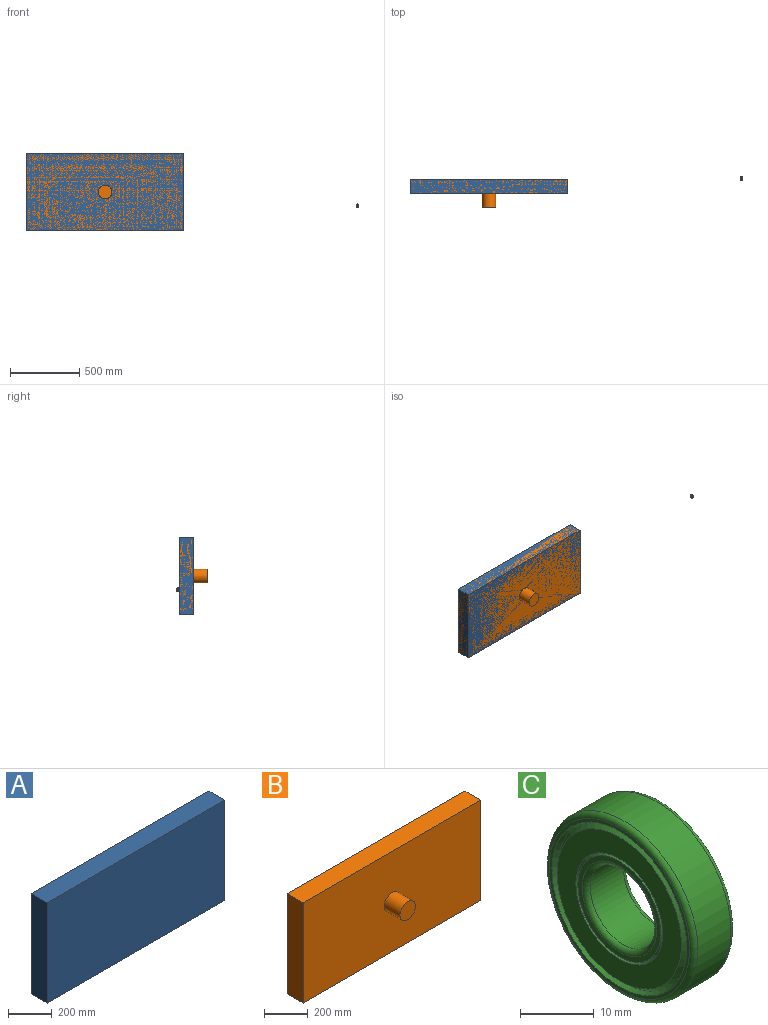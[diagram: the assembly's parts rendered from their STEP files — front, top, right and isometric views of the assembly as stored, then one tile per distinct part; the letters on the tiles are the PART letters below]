
ASSEMBLY  parts=3 mates=2
PART A: 6 faces, bbox 1143x101.6x558.8 mm
  f0: plane 558.8x101.6mm, normal (-1,0,0), area 56774.1mm2, adj f1,f3,f4,f5
  f1: plane 1143x101.6mm, normal (0,0,-1), area 116128.8mm2, adj f0,f2,f4,f5
  f2: plane 558.8x101.6mm, normal (1,0,0), area 56774.1mm2, adj f1,f3,f4,f5
  f3: plane 1143x101.6mm, normal (0,0,1), area 116128.8mm2, adj f0,f2,f4,f5
  f4: plane 1143x558.8mm, normal (0,-1,0), area 638708.4mm2, adj f0,f1,f2,f3
  f5: plane 1143x558.8mm, normal (0,1,0), area 638708.4mm2, adj f0,f1,f2,f3
PART B: 8 faces, bbox 1143x203.2x558.8 mm
  f0: plane 558.8x101.6mm, normal (-1,0,0), area 56774.1mm2, adj f1,f3,f4,f5
  f1: plane 1143x101.6mm, normal (0,0,-1), area 116128.8mm2, adj f0,f2,f4,f5
  f2: plane 558.8x101.6mm, normal (1,0,0), area 56774.1mm2, adj f1,f3,f4,f5
  f3: plane 1143x101.6mm, normal (0,0,1), area 116128.8mm2, adj f0,f2,f4,f5
  f4: plane 1143x558.8mm, normal (0,-1,0), area 630867.7mm2, adj f0,f1,f2,f3,f6
  f5: plane 1143x558.8mm, normal (0,1,0), area 638708.4mm2, adj f0,f1,f2,f3
  f6: cylinder r=49.96mm len=101.6mm, axis (0,1,0), area 31891.6mm2, adj f4,f7
  f7: plane 99.92x99.92mm, normal (0,-1,0), area 7840.7mm2, adj f6
PART C: 20 faces, bbox 7.9x30.9x30.9 mm
  f0: cone r=12.95mm half-angle=27.8deg, axis (1,0,0), area 65.6mm2, adj f1,f15
  f1: cone r=12.57mm half-angle=41.3deg, axis (-1,0,0), area 74.1mm2, adj f0,f14
  f2: cone r=7.97mm half-angle=26.6deg, axis (-1,0,0), area 21.6mm2, adj f3,f18
  f3: cone r=8.16mm half-angle=26.6deg, axis (1,0,0), area 22.1mm2, adj f2,f14
  f4: cone r=12.95mm half-angle=27.8deg, axis (-1,0,0), area 65.6mm2, adj f5,f17
  f5: cone r=12.57mm half-angle=41.3deg, axis (1,0,0), area 74.1mm2, adj f4,f16
  f6: cone r=7.97mm half-angle=26.6deg, axis (1,0,0), area 21.6mm2, adj f7,f19
  f7: cone r=8.16mm half-angle=26.6deg, axis (-1,0,0), area 22.1mm2, adj f6,f16
  f8: torus R=13.49mm, axis (1,0,0), area 109.7mm2, adj f13,f15
  f9: torus R=7.14mm, axis (1,0,0), area 52mm2, adj f12,f18
  f10: torus R=7.14mm, axis (1,0,0), area 52mm2, adj f12,f19
  f11: torus R=13.49mm, axis (1,0,0), area 109.7mm2, adj f13,f17
  f12: cylinder r=6.35mm len=12.7mm, axis (1,0,0), area 253.4mm2, adj f9,f10
  f13: cylinder r=14.29mm len=28.58mm, axis (-1,0,0), area 570mm2, adj f8,f11
  f14: plane 23.88x23.88mm, normal (1,0,0), area 228.6mm2, adj f1,f3
  f15: plane 26.99x26.99mm, normal (1,0,0), area 44.8mm2, adj f0,f8
  f16: plane 23.88x23.88mm, normal (-1,0,0), area 228.6mm2, adj f5,f7
  f17: plane 26.99x26.99mm, normal (-1,0,0), area 44.8mm2, adj f4,f11
  f18: plane 15.94x15.94mm, normal (1,0,0), area 39.3mm2, adj f2,f9
  f19: plane 15.94x15.94mm, normal (-1,0,0), area 39.3mm2, adj f6,f10
PLACE A rot(axis=(0,1,0),180deg) t=(-1781.45,11.09,-52.99)mm
PLACE B t=(-1781.45,11.09,-52.99)mm
PLACE C t=(101.7,0,-168.67)mm
MATE parallel A.f0 <-> B.f0  axis (1,0,0) through (-1209.95,-39.71,-52.99)mm
MATE pin_slot B.f0 <-> A.f2  axis (-1,0,0) through (-2352.95,-39.71,-52.99)mm
